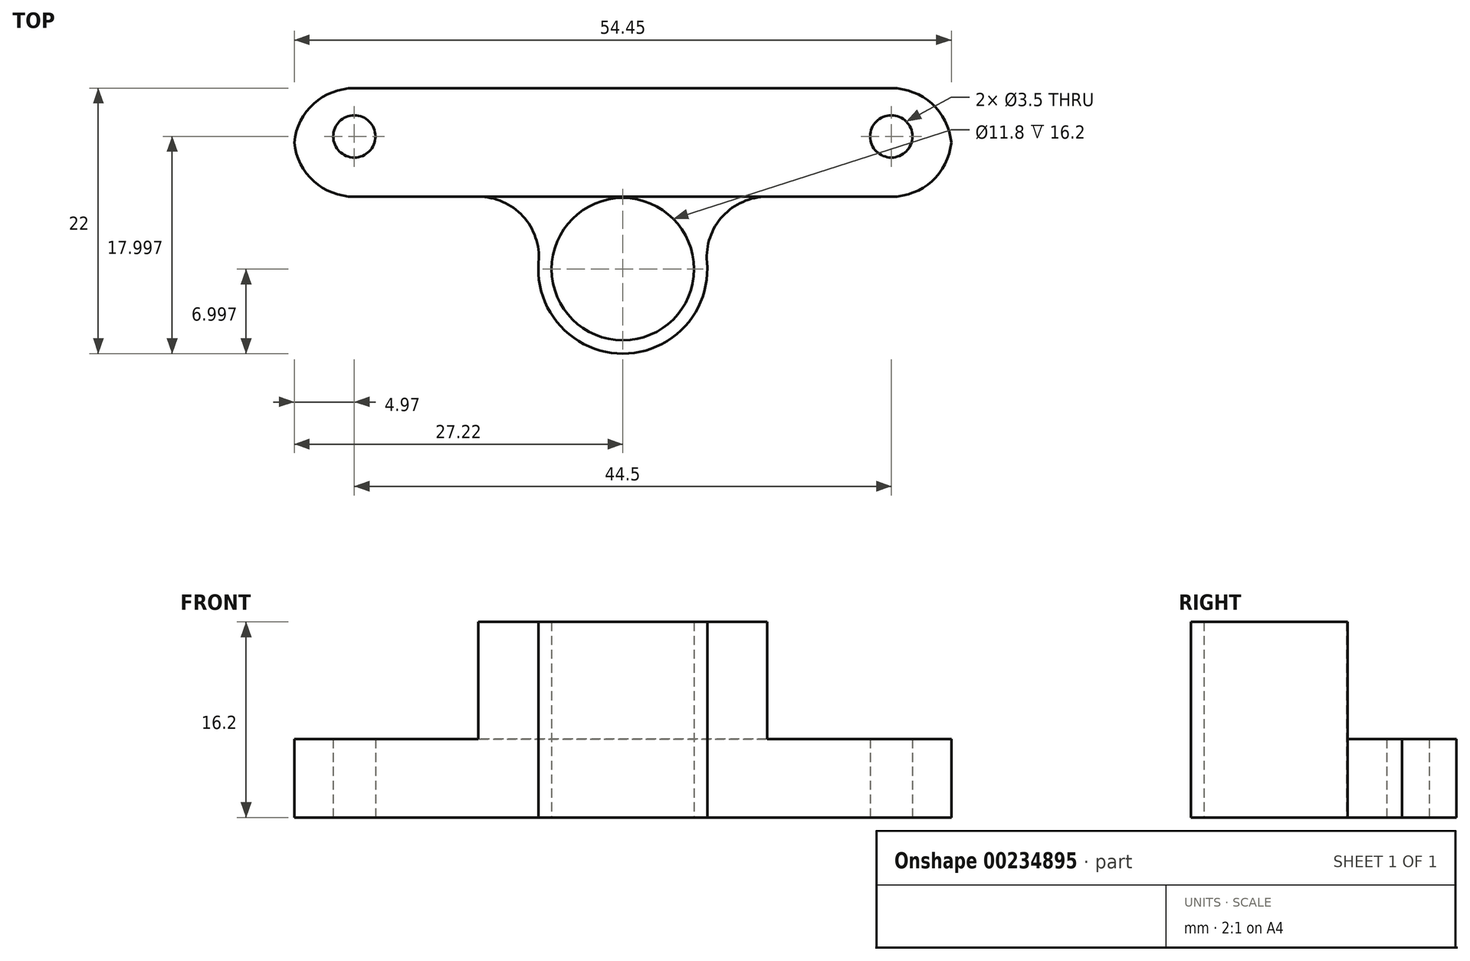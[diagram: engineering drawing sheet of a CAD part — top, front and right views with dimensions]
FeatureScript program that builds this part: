
annotation { "Feature Type Name" : "Feature", "Feature Type Description" : "" }
export const myFeature = defineFeature(function(context is Context, id is Id, definition is map)
    precondition{}
    {
        {
            var Q0;
            Q0=qCreatedBy(makeId("Top.planeOp"),FACE);
            var sketch = newSketch(context, id + "F0", { "sketchPlane" : qUnion([Q0])});
            skCircle(sketch, "E0", {"center": v(-36.72, 16.46) * mm, "radius": 1.75 * mm});
            skCircle(sketch, "E1", {"center": v(7.78, 16.46) * mm, "radius": 1.75 * mm});
            skLineSegment(sketch, "E2.bottom", {"start": v(-36.72, 20.46) * mm, "end": v(7.78, 20.46) * mm});
            skLineSegment(sketch, "E2.top", {"start": v(-36.72, 11.46) * mm, "end": v(-26.43, 11.46) * mm});
            skLineSegment(sketch, "E2.left", {"start": v(-41.72, 16.46) * mm, "end": v(-41.72, 15.46) * mm});
            skLineSegment(sketch, "E2.right", {"start": v(12.78, 16.46) * mm, "end": v(12.78, 15.46) * mm});
            skCircle(sketch, "E3", {"center": v(-14.47, 5.46) * mm, "radius": 5.9 * mm});
            skArc(sketch, "E4", {"start": v(-21.45, 6.04) * mm, "mid": v(-14.47, -1.54) * mm, "end": v(-7.5, 6.04) * mm});
            skLineSegment(sketch, "E5.trimOffspring", {"start": v(-2.51, 11.46) * mm, "end": v(7.78, 11.46) * mm});
            skPoint(sketch, "E6.visualSharp", {"position": v(-10.86, 11.46) * mm});
            skArc(sketch, "E6.filletArc", {"start": v(-2.51, 11.46) * mm, "mid": v(-6.2, 9.84) * mm, "end": v(-7.5, 6.04) * mm});
            skPoint(sketch, "E7.visualSharp", {"position": v(-18.08, 11.46) * mm});
            skArc(sketch, "E7.filletArc", {"start": v(-21.45, 6.04) * mm, "mid": v(-22.75, 9.84) * mm, "end": v(-26.43, 11.46) * mm});
            skPoint(sketch, "E8.visualSharp", {"position": v(-41.72, 20.46) * mm});
            skArc(sketch, "E8.filletArc", {"start": v(-36.72, 20.46) * mm, "mid": v(-40.26, 19) * mm, "end": v(-41.72, 15.46) * mm});
            skPoint(sketch, "E9.visualSharp", {"position": v(-41.72, 11.46) * mm});
            skArc(sketch, "E9.filletArc", {"start": v(-41.72, 16.46) * mm, "mid": v(-40.26, 12.92) * mm, "end": v(-36.72, 11.46) * mm});
            skPoint(sketch, "E10.visualSharp", {"position": v(12.78, 20.46) * mm});
            skArc(sketch, "E10.filletArc", {"start": v(12.78, 15.46) * mm, "mid": v(11.32, 19) * mm, "end": v(7.78, 20.46) * mm});
            skPoint(sketch, "E11.visualSharp", {"position": v(12.78, 11.46) * mm});
            skArc(sketch, "E11.filletArc", {"start": v(7.78, 11.46) * mm, "mid": v(11.32, 12.92) * mm, "end": v(12.78, 16.46) * mm});
            skLineSegment(sketch, "E12", {"start": v(-26.43, 11.46) * mm, "end": v(-2.51, 11.46) * mm});
            skLineSegment(sketch, "E13.top", {"start": v(-36.72, 11.46) * mm, "end": v(7.78, 11.46) * mm});
            skPoint(sketch, "E14.orphan", {"position": v(29.52, 11.46) * mm});
            skSolve(sketch);
        }
        {
            var Q0;
            Q0=makeQuery(id+"F0.imprint","IMPRINT",FACE,{"disambiguationData":[TD([[makeQuery(id+"F0.imprint","IMPRINT",EDGE,{"derivedFrom":sQuery(id+"F0.wireOp",EDGE,"E0")}),-1.0]])]});
            var Q1;
            {var subQ2=sQuery(id+"F0.wireOp",EDGE,"E3");Q1=makeQuery(id+"F0.imprint","IMPRINT",FACE,{"disambiguationData":[TD([[makeQuery(id+"F0.imprint","IMPRINT",EDGE,{"derivedFrom":subQ2}),-1.0]])]});}
            extrude(context, id + "F1", {"entities" : qUnion([Q0, Q1]), "depth" : 6.5 * mm});
        }
        {
            var Q0;
            Q0=makeQuery(id+"F0.imprint","IMPRINT",FACE,{"disambiguationData":[TD([[makeQuery(id+"F0.imprint","IMPRINT",EDGE,{"derivedFrom":sQuery(id+"F0.wireOp",EDGE,"E3")}),-1.0]])]});
            extrude(context, id + "F2", {"entities" : qUnion([Q0]), "operationType" : NewBodyOperationType.ADD, "depth" : 16.2 * mm});
        }
    });
